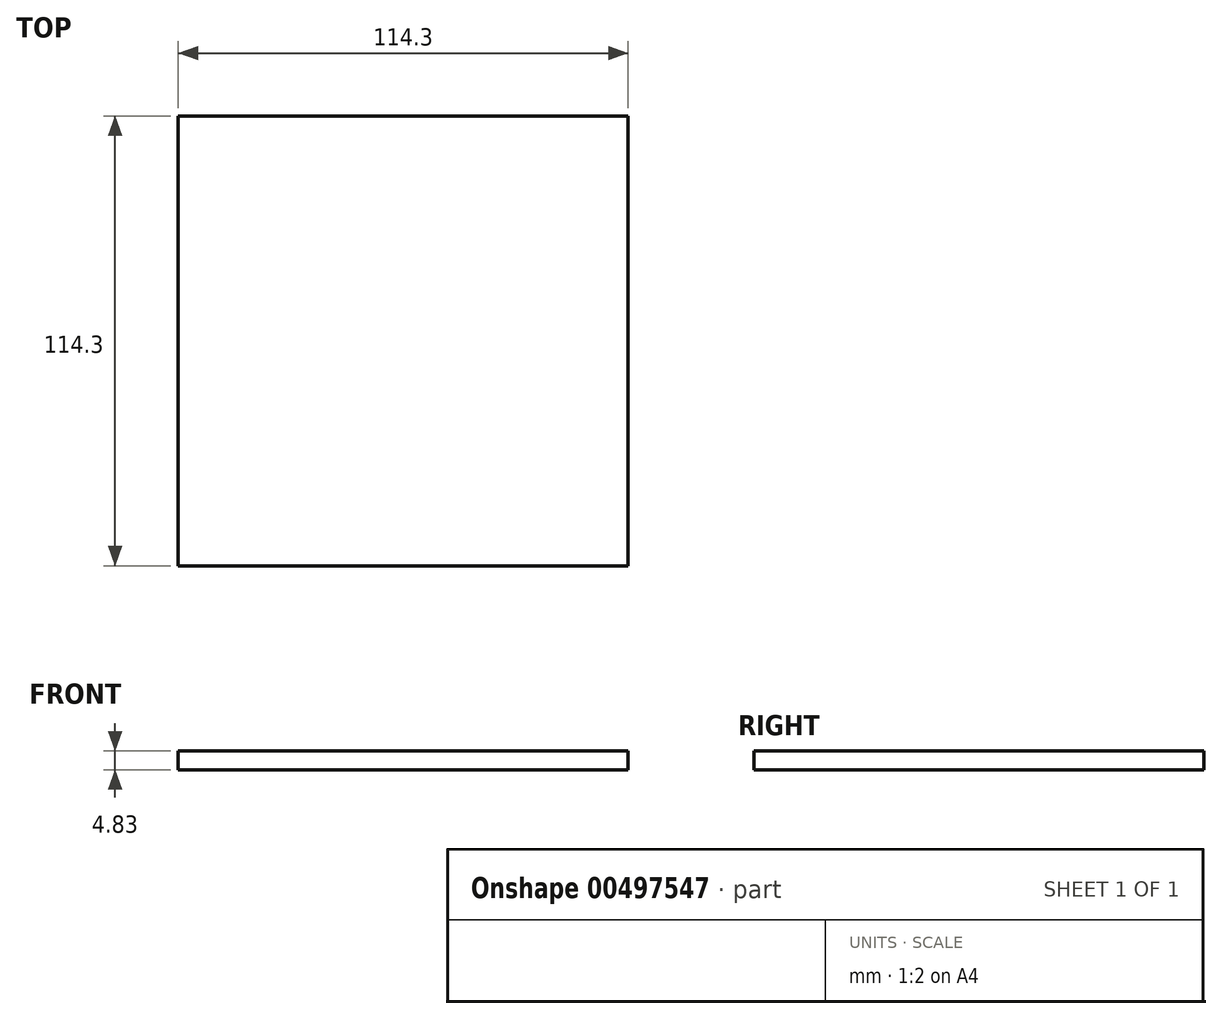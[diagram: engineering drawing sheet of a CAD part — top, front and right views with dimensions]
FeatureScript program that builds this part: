
annotation { "Feature Type Name" : "Feature", "Feature Type Description" : "" }
export const myFeature = defineFeature(function(context is Context, id is Id, definition is map)
    precondition{}
    {
        {
            var Q0;
            Q0=qCreatedBy(makeId("Top.planeOp"),FACE);
            var sketch = newSketch(context, id + "F0", { "sketchPlane" : qUnion([Q0])});
            skLineSegment(sketch, "E0.bottom", {"start": v(-57.15, 57.15) * mm, "end": v(57.15, 57.15) * mm});
            skLineSegment(sketch, "E0.top", {"start": v(-57.15, -57.15) * mm, "end": v(57.15, -57.15) * mm});
            skLineSegment(sketch, "E0.left", {"start": v(-57.15, 57.15) * mm, "end": v(-57.15, -57.15) * mm});
            skLineSegment(sketch, "E0.right", {"start": v(57.15, 57.15) * mm, "end": v(57.15, -57.15) * mm});
            skPoint(sketch, "E0.middle", {"position": v(0, 0) * mm});
            skSolve(sketch);
        }
        {
            var Q0;
            Q0 = qSketchRegion(id + "F0", true);
            extrude(context, id + "F1", {"entities" : qUnion([Q0]), "depth" : 4.83 * mm});
        }
    });
